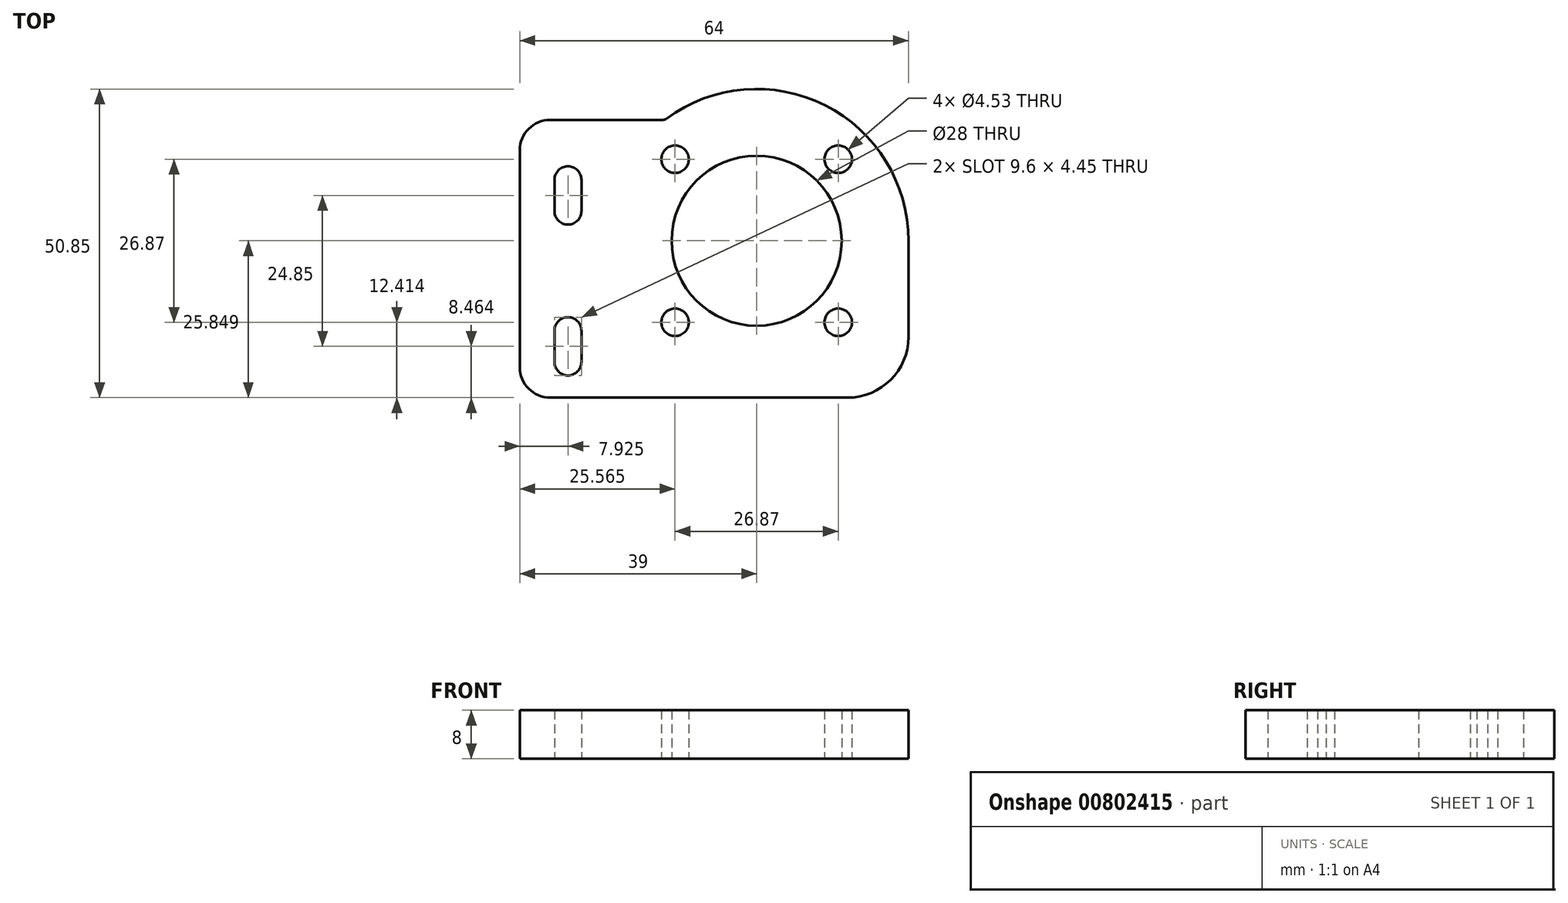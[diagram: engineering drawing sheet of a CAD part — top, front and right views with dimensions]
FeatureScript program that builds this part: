
annotation { "Feature Type Name" : "Feature", "Feature Type Description" : "" }
export const myFeature = defineFeature(function(context is Context, id is Id, definition is map)
    precondition{}
    {
        {
            var Q0;
            Q0=qCreatedBy(makeId("Top.planeOp"),FACE);
            var sketch = newSketch(context, id + "F0", { "sketchPlane" : qUnion([Q0])});
            skLineSegment(sketch, "E0.bottom", {"start": v(-106.95, 1.5) * mm, "end": v(-88.38, 1.5) * mm});
            skLineSegment(sketch, "E0.left", {"start": v(-111.95, -3.5) * mm, "end": v(-111.95, -39.27) * mm});
            skLineSegment(sketch, "E1", {"start": v(-41.95, 1.5) * mm, "end": v(-41.95, -48.27) * mm, "construction": true});
            skLineSegment(sketch, "E2.MirrorCS", {"start": v(-101.8, -38.38) * mm, "end": v(-101.8, -33.23) * mm});
            skArc(sketch, "E3.MirrorCS", {"start": v(-106.25, -38.38) * mm, "mid": v(-104.02, -40.6) * mm, "end": v(-101.8, -38.38) * mm});
            skLineSegment(sketch, "E4.MirrorCS", {"start": v(-106.25, -38.38) * mm, "end": v(-106.25, -33.23) * mm});
            skArc(sketch, "E5.MirrorCS", {"start": v(-101.8, -33.23) * mm, "mid": v(-104.02, -31) * mm, "end": v(-106.25, -33.23) * mm});
            skLineSegment(sketch, "E6.MirrorCS", {"start": v(-101.8, -13.53) * mm, "end": v(-106.25, -13.53) * mm, "construction": true});
            skLineSegment(sketch, "E7.MirrorCS", {"start": v(-104.02, 1.5) * mm, "end": v(-104.02, -48.27) * mm, "construction": true});
            skLineSegment(sketch, "E8.MirrorCS", {"start": v(-101.8, -8.38) * mm, "end": v(-106.25, -8.38) * mm, "construction": true});
            skLineSegment(sketch, "E9.MirrorCS", {"start": v(-106.25, -8.38) * mm, "end": v(-106.25, -13.53) * mm});
            skArc(sketch, "E10.MirrorCS", {"start": v(-106.25, -8.38) * mm, "mid": v(-104.02, -6.16) * mm, "end": v(-101.8, -8.38) * mm});
            skLineSegment(sketch, "E11.MirrorCS", {"start": v(-101.8, -8.38) * mm, "end": v(-101.8, -13.53) * mm});
            skArc(sketch, "E12.MirrorCS", {"start": v(-101.8, -13.53) * mm, "mid": v(-104.02, -15.76) * mm, "end": v(-106.25, -13.53) * mm});
            skCircle(sketch, "E13.MirrorC", {"center": v(-72.95, -18.42) * mm, "radius": 14 * mm});
            skCircle(sketch, "E14.MirrorC", {"center": v(-86.38, -31.86) * mm, "radius": 2.27 * mm});
            skCircle(sketch, "E15.MirrorC", {"center": v(-59.51, -31.86) * mm, "radius": 2.27 * mm});
            skCircle(sketch, "E16.MirrorC", {"center": v(-59.51, -4.99) * mm, "radius": 2.27 * mm});
            skCircle(sketch, "E17.MirrorC", {"center": v(-86.38, -4.99) * mm, "radius": 2.27 * mm});
            skPoint(sketch, "E18.visualSharp", {"position": v(-111.95, 1.5) * mm});
            skArc(sketch, "E18.filletArc", {"start": v(-106.95, 1.5) * mm, "mid": v(-110.49, 0.04) * mm, "end": v(-111.95, -3.5) * mm});
            skPoint(sketch, "E19.visualSharp", {"position": v(-111.95, -48.27) * mm});
            skArc(sketch, "E20", {"start": v(-47.95, -18.42) * mm, "mid": v(-61.68, 3.9) * mm, "end": v(-87.79, 1.7) * mm});
            skLineSegment(sketch, "E21.trimOffspring", {"start": v(-84.72, -44.27) * mm, "end": v(-57.95, -44.27) * mm});
            skPoint(sketch, "E22.visualSharp", {"position": v(-111.95, -69.27) * mm});
            skPoint(sketch, "E23.visualSharp", {"position": v(-95, -69.27) * mm});
            skPoint(sketch, "E24.visualSharp", {"position": v(-85.4, -44.27) * mm});
            skPoint(sketch, "E25.visualSharp", {"position": v(-57.85, 1.5) * mm});
            skPoint(sketch, "E26.visualSharp", {"position": v(-88.05, 1.5) * mm});
            skArc(sketch, "E26.filletArc", {"start": v(-88.38, 1.5) * mm, "mid": v(-88.07, 1.55) * mm, "end": v(-87.79, 1.7) * mm});
            skLineSegment(sketch, "E27", {"start": v(-84.72, -44.27) * mm, "end": v(-106.95, -44.27) * mm});
            skPoint(sketch, "E28.visualSharp", {"position": v(-111.95, -44.27) * mm});
            skArc(sketch, "E28.filletArc", {"start": v(-111.95, -39.27) * mm, "mid": v(-110.49, -42.8) * mm, "end": v(-106.95, -44.27) * mm});
            skLineSegment(sketch, "E29", {"start": v(-47.95, -18.42) * mm, "end": v(-47.95, -34.27) * mm});
            skArc(sketch, "E30.filletArc", {"start": v(-57.95, -44.27) * mm, "mid": v(-50.88, -41.34) * mm, "end": v(-47.95, -34.27) * mm});
            skArc(sketch, "E31.MirrorCS", {"start": v(4.48, 1.5) * mm, "mid": v(4.17, 1.55) * mm, "end": v(3.89, 1.7) * mm});
            skLineSegment(sketch, "E32.MirrorCS", {"start": v(17.9, -8.38) * mm, "end": v(17.9, -13.53) * mm});
            skLineSegment(sketch, "E33.MirrorCS", {"start": v(17.9, -8.38) * mm, "end": v(22.35, -8.38) * mm, "construction": true});
            skLineSegment(sketch, "E34.MirrorCS", {"start": v(17.9, -13.53) * mm, "end": v(22.35, -13.53) * mm, "construction": true});
            skLineSegment(sketch, "E35.MirrorCS", {"start": v(22.35, -38.38) * mm, "end": v(22.35, -33.23) * mm});
            skArc(sketch, "E36.MirrorCS", {"start": v(17.9, -13.53) * mm, "mid": v(20.13, -15.76) * mm, "end": v(22.35, -13.53) * mm});
            skArc(sketch, "E37.MirrorCS", {"start": v(22.35, -8.38) * mm, "mid": v(20.13, -6.16) * mm, "end": v(17.9, -8.38) * mm});
            skLineSegment(sketch, "E38.MirrorCS", {"start": v(22.35, -8.38) * mm, "end": v(22.35, -13.53) * mm});
            skArc(sketch, "E39.MirrorCS", {"start": v(23.05, 1.5) * mm, "mid": v(26.59, 0.04) * mm, "end": v(28.05, -3.5) * mm});
            skArc(sketch, "E40.MirrorCS", {"start": v(22.35, -38.38) * mm, "mid": v(20.13, -40.6) * mm, "end": v(17.9, -38.38) * mm});
            skLineSegment(sketch, "E41.MirrorCS", {"start": v(17.9, -38.38) * mm, "end": v(17.9, -33.23) * mm});
            skArc(sketch, "E42.MirrorCS", {"start": v(28.05, -39.27) * mm, "mid": v(26.59, -42.8) * mm, "end": v(23.05, -44.27) * mm});
            skArc(sketch, "E43.MirrorCS", {"start": v(17.9, -33.23) * mm, "mid": v(20.13, -31) * mm, "end": v(22.35, -33.23) * mm});
            skCircle(sketch, "E44.MirrorC", {"center": v(-24.38, -31.86) * mm, "radius": 2.27 * mm});
            skCircle(sketch, "E45.MirrorC", {"center": v(2.49, -31.86) * mm, "radius": 2.27 * mm});
            skCircle(sketch, "E46.MirrorC", {"center": v(2.49, -4.99) * mm, "radius": 2.27 * mm});
            skCircle(sketch, "E47.MirrorC", {"center": v(-24.38, -4.99) * mm, "radius": 2.27 * mm});
            skLineSegment(sketch, "E48.MirrorCS", {"start": v(23.05, 1.5) * mm, "end": v(4.48, 1.5) * mm});
            skPoint(sketch, "E49.MirrorP", {"position": v(28.05, 1.5) * mm});
            skPoint(sketch, "E50.MirrorP", {"position": v(1.5, -44.27) * mm});
            skArc(sketch, "E51.MirrorCS", {"start": v(-35.95, -18.42) * mm, "mid": v(-22.22, 3.9) * mm, "end": v(3.89, 1.7) * mm});
            skLineSegment(sketch, "E52.MirrorCS", {"start": v(0.82, -44.27) * mm, "end": v(23.05, -44.27) * mm});
            skCircle(sketch, "E53.MirrorC", {"center": v(-10.95, -18.42) * mm, "radius": 14 * mm});
            skArc(sketch, "E54.MirrorCS", {"start": v(-25.95, -44.27) * mm, "mid": v(-33.02, -41.34) * mm, "end": v(-35.95, -34.27) * mm});
            skLineSegment(sketch, "E55.MirrorCS", {"start": v(28.05, -3.5) * mm, "end": v(28.05, -39.27) * mm});
            skLineSegment(sketch, "E56.MirrorCS", {"start": v(-35.95, -18.42) * mm, "end": v(-35.95, -34.27) * mm});
            skPoint(sketch, "E57.MirrorP", {"position": v(-26.05, 1.5) * mm});
            skLineSegment(sketch, "E58.MirrorCS", {"start": v(0.82, -44.27) * mm, "end": v(-25.95, -44.27) * mm});
            skPoint(sketch, "E59.MirrorP", {"position": v(28.05, -44.27) * mm});
            skPoint(sketch, "E60.MirrorP", {"position": v(4.15, 1.5) * mm});
            skSolve(sketch);
        }
        {
            var Q0;
            Q0=makeQuery(id+"F0.imprint","IMPRINT",FACE,{"disambiguationData":[TD([[makeQuery(id+"F0.imprint","IMPRINT",EDGE,{"derivedFrom":sQuery(id+"F0.wireOp",EDGE,"E0.bottom")}),-1.0]])]});
            var Q1;
            Q1=makeQuery(id+"F0.imprint","IMPRINT",FACE,{"disambiguationData":[TD([[makeQuery(id+"F0.imprint","IMPRINT",EDGE,{"derivedFrom":sQuery(id+"F0.wireOp",EDGE,"E31.MirrorCS")}),1.0]])]});
            extrude(context, id + "F1", {"entities" : qUnion([Q0, Q1]), "depth" : 8 * mm, "offsetDistance" : 25 * mm});
        }
    });
